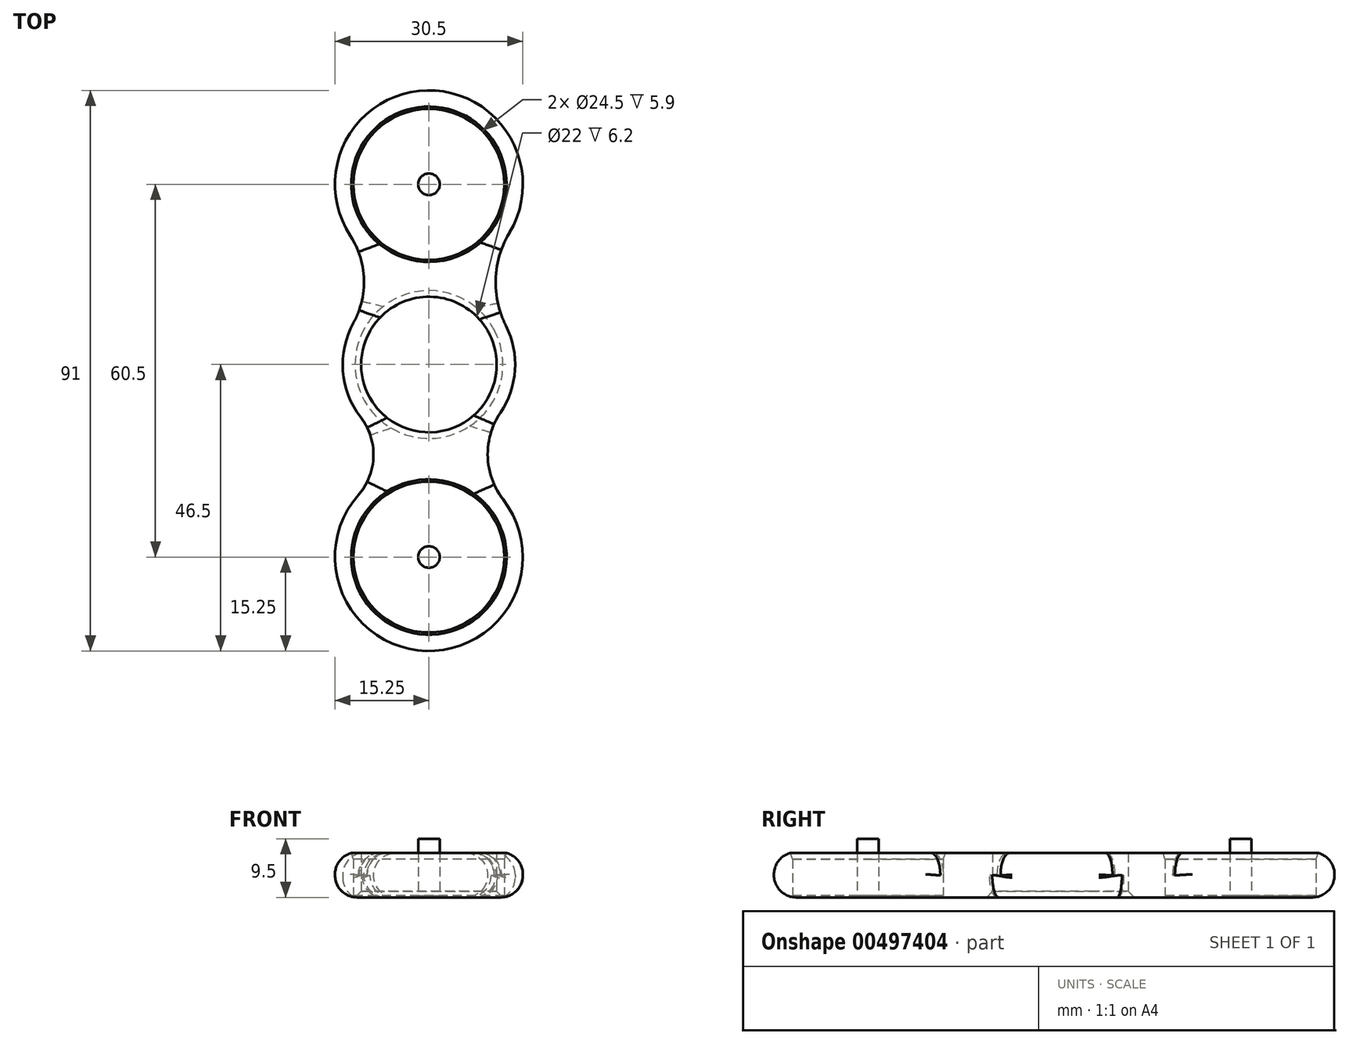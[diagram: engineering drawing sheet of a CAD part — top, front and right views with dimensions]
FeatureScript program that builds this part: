
annotation { "Feature Type Name" : "Feature", "Feature Type Description" : "" }
export const myFeature = defineFeature(function(context is Context, id is Id, definition is map)
    precondition{}
    {
        {
            assignVariable(context, id + "F0", {"name" : "bearing_thickness", "anyValue" : 7.2});
        }
        {
            var Q0;
            Q0=qCreatedBy(makeId("Top.planeOp"),FACE);
            var sketch = newSketch(context, id + "F1", { "sketchPlane" : qUnion([Q0])});
            skCircle(sketch, "E0", {"center": v(0, 0) * mm, "radius": 11 * mm});
            skCircle(sketch, "E1", {"center": v(0, 29.25) * mm, "radius": 12.25 * mm});
            skArc(sketch, "E2", {"start": v(13.08, 21.4) * mm, "mid": v(-0.29, 44.5) * mm, "end": v(-12.77, 20.92) * mm});
            skArc(sketch, "E3", {"start": v(-12.25, 6.77) * mm, "mid": v(-13.96, -1.07) * mm, "end": v(-11.08, -8.56) * mm});
            skArc(sketch, "E4", {"start": v(-12.25, 6.77) * mm, "mid": v(-10.55, 13.92) * mm, "end": v(-12.77, 20.92) * mm});
            skArc(sketch, "E5", {"start": v(13.08, 21.4) * mm, "mid": v(10.85, 13.92) * mm, "end": v(12.5, 6.29) * mm});
            skCircle(sketch, "E6", {"center": v(0, -31.25) * mm, "radius": 12.25 * mm});
            skArc(sketch, "E7", {"start": v(-11.47, -21.2) * mm, "mid": v(-0.46, -46.5) * mm, "end": v(12.05, -21.9) * mm});
            skArc(sketch, "E8", {"start": v(-11.47, -21.2) * mm, "mid": v(-9, -14.95) * mm, "end": v(-11.08, -8.56) * mm});
            skArc(sketch, "E9", {"start": v(11.6, -7.85) * mm, "mid": v(9.54, -14.95) * mm, "end": v(12.05, -21.9) * mm});
            skArc(sketch, "E10.trimOffspring", {"start": v(11.6, -7.85) * mm, "mid": v(13.97, -0.9) * mm, "end": v(12.5, 6.29) * mm});
            skSolve(sketch);
        }
        {
            var Q0;
            Q0=makeQuery(id+"F1.imprint","IMPRINT",FACE,{"disambiguationData":[TD([[makeQuery(id+"F1.imprint","IMPRINT",EDGE,{"derivedFrom":sQuery(id+"F1.wireOp",EDGE,"E0")}),-1.0]])]});
            extrude(context, id + "F2", {"entities" : qUnion([Q0]), "depth" : (getVariable(context, 'bearing_thickness')) * mm});
        }
        {
            var Q0;
            Q0=makeQuery(id+"F2.opExtrude","CAP_FACE",FACE,{"disambiguationData":[OSD([sQuery(id+"F1.wireOp",EDGE,"E0"),sQuery(id+"F1.wireOp",EDGE,"E1"),sQuery(id+"F1.wireOp",EDGE,"E2"),sQuery(id+"F1.wireOp",EDGE,"E3"),sQuery(id+"F1.wireOp",EDGE,"E4"),sQuery(id+"F1.wireOp",EDGE,"E5"),sQuery(id+"F1.wireOp",EDGE,"E6"),sQuery(id+"F1.wireOp",EDGE,"E7"),sQuery(id+"F1.wireOp",EDGE,"E8"),sQuery(id+"F1.wireOp",EDGE,"E9"),sQuery(id+"F1.wireOp",EDGE,"E10.trimOffspring")])],"isStart":true});
            var sketch = newSketch(context, id + "F3", { "sketchPlane" : qUnion([Q0])});
            skCircle(sketch, "E11", {"center": v(0, 31.25) * mm, "radius": 12.25 * mm});
            skCircle(sketch, "E12", {"center": v(0, -29.25) * mm, "radius": 12.25 * mm});
            skSolve(sketch);
        }
        {
            var Q0;
            Q0=makeQuery(id+"F3.imprint","IMPRINT",FACE,{"disambiguationData":[TD([[makeQuery(id+"F3.imprint","IMPRINT",EDGE,{"derivedFrom":sQuery(id+"F3.wireOp",EDGE,"E11")}),-1.0]])]});
            var Q1;
            Q1=makeQuery(id+"F3.imprint","IMPRINT",FACE,{"disambiguationData":[TD([[makeQuery(id+"F3.imprint","IMPRINT",EDGE,{"derivedFrom":sQuery(id+"F3.wireOp",EDGE,"E12")}),-1.0]])]});
            extrude(context, id + "F4", {"entities" : qUnion([Q0, Q1]), "operationType" : NewBodyOperationType.ADD, "oppositeDirection" : true, "depth" : 0.3 * mm});
        }
        {
            var Q0;
            Q0=makeQuery(id+"F4.opExtrude","CAP_FACE",FACE,{"disambiguationData":[OSD([sQuery(id+"F3.wireOp",EDGE,"E11")])],"isStart":false});
            var sketch = newSketch(context, id + "F5", { "sketchPlane" : qUnion([Q0])});
            skCircle(sketch, "E13", {"center": v(0, -31.25) * mm, "radius": 1.75 * mm});
            skCircle(sketch, "E14", {"center": v(0, 29.25) * mm, "radius": 1.75 * mm});
            skSolve(sketch);
        }
        {
            var Q0;
            Q0=makeQuery(id+"F5.imprint","IMPRINT",FACE,{"disambiguationData":[TD([[makeQuery(id+"F5.imprint","IMPRINT",EDGE,{"derivedFrom":sQuery(id+"F5.wireOp",EDGE,"E14")}),1.0]])]});
            var Q1;
            Q1=makeQuery(id+"F5.imprint","IMPRINT",FACE,{"disambiguationData":[TD([[makeQuery(id+"F5.imprint","IMPRINT",EDGE,{"derivedFrom":sQuery(id+"F5.wireOp",EDGE,"E13")}),1.0]])]});
            extrude(context, id + "F6", {"entities" : qUnion([Q0, Q1]), "operationType" : NewBodyOperationType.ADD, "depth" : (getVariable(context, 'bearing_thickness') + 2) * mm});
        }
        {
            var Q0;
            Q0=makeQuery(id+"F2.opExtrude","CAP_EDGE",EDGE,{"disambiguationData":[OSD([sQuery(id+"F1.wireOp",EDGE,"E1")])],"isStart":false});
            var Q1;
            Q1=makeQuery(id+"F2.opExtrude","CAP_EDGE",EDGE,{"disambiguationData":[OSD([sQuery(id+"F1.wireOp",EDGE,"E6")])],"isStart":false});
            chamfer(context, id + "F7", {"entities" : qUnion([Q0, Q1]), "chamferType" : ChamferType.OFFSET_ANGLE, "width" : 1 * mm, "oppositeDirection" : false, "angle" : 20 * degree, "tangentPropagation" : true});
        }
        {
            var Q0;
            Q0=makeQuery(id+"F2.opExtrude","CAP_EDGE",EDGE,{"disambiguationData":[OSD([sQuery(id+"F1.wireOp",EDGE,"E0")])],"isStart":true});
            chamfer(context, id + "F8", {"entities" : qUnion([Q0]), "width" : 1 * mm, "tangentPropagation" : true});
        }
        {
            var Q0;
            Q0=makeQuery(id+"F2.opExtrude","CAP_EDGE",EDGE,{"disambiguationData":[OSD([sQuery(id+"F1.wireOp",EDGE,"E2")])],"isStart":false});
            var Q1;
            Q1=makeQuery(id+"F2.opExtrude","CAP_EDGE",EDGE,{"disambiguationData":[OSD([sQuery(id+"F1.wireOp",EDGE,"E2")])],"isStart":true});
            fillet(context, id + "F9", {"entities" : qUnion([Q0, Q1]), "radius" : (getVariable(context, 'bearing_thickness') / 2) * mm, "tangentPropagation" : true, "allowEdgeOverflow" : false});
        }
    });
